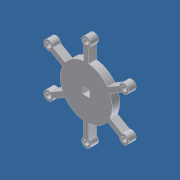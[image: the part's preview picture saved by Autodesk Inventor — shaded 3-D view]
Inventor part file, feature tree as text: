
AUTODESK INVENTOR PART (.ipt)
format: ipt  version: unknown  size: 223,744 bytes
history: native  units: in
note: dims shown in document units (in); Inventor stores cm internally (conversion verified against a paired STEP export)
features: extrude x1, sketch x1
ambient origin geometry x8: Origin, YZ Plane, XZ Plane, XY Plane, X Axis, Y Axis, Z Axis, Center Point
feature tree (2):
  extrude  "Extrusion5"  Depth=0.376in
  sketch  "Sketch1"  dims[d0=1.625in d6=0.376in d43=0.163in d44=0.0in]
